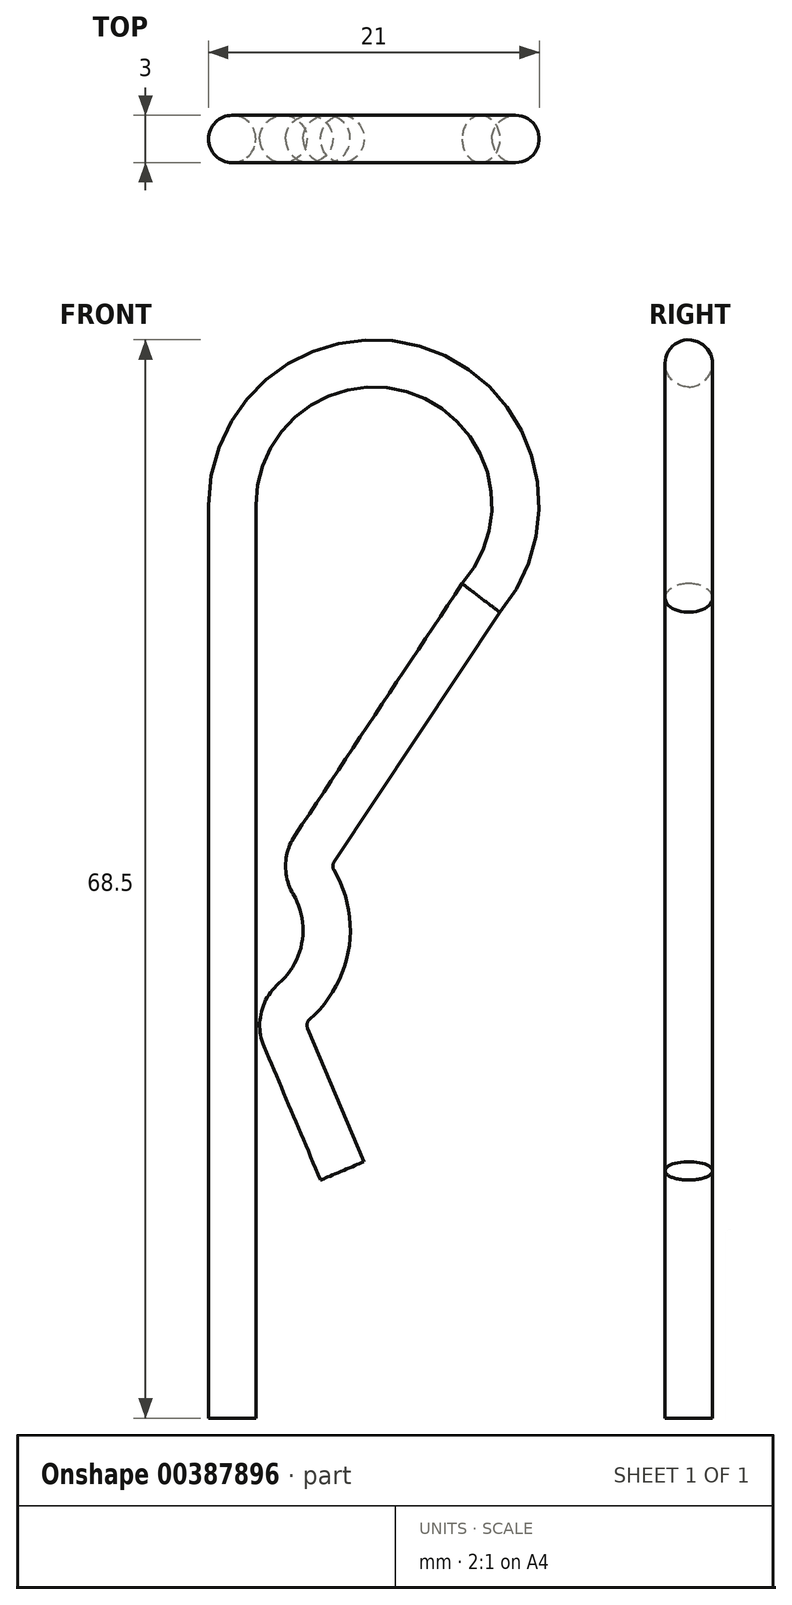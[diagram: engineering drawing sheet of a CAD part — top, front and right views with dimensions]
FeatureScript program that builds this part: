
annotation { "Feature Type Name" : "Feature", "Feature Type Description" : "" }
export const myFeature = defineFeature(function(context is Context, id is Id, definition is map)
    precondition{}
    {
        {
            var Q0;
            Q0=qCreatedBy(makeId("Front.planeOp"),FACE);
            var sketch = newSketch(context, id + "F0", { "sketchPlane" : qUnion([Q0])});
            skArc(sketch, "E0", {"start": v(15.8, 52.1) * mm, "mid": v(12.15, 66.43) * mm, "end": v(0, 58) * mm});
            skLineSegment(sketch, "E1", {"start": v(15.8, 52.1) * mm, "end": v(5.22, 36.17) * mm});
            skLineSegment(sketch, "E2", {"start": v(3.4, 24.18) * mm, "end": v(7, 15.7) * mm});
            skArc(sketch, "E3", {"start": v(3.94, 26.47) * mm, "mid": v(5.92, 30.04) * mm, "end": v(5.17, 34.05) * mm});
            skPoint(sketch, "E4.visualSharp", {"position": v(4.46, 35.01) * mm});
            skArc(sketch, "E4.filletArc", {"start": v(5.22, 36.17) * mm, "mid": v(4.9, 35.12) * mm, "end": v(5.17, 34.05) * mm});
            skPoint(sketch, "E5.visualSharp", {"position": v(2.77, 25.68) * mm});
            skArc(sketch, "E5.filletArc", {"start": v(3.94, 26.47) * mm, "mid": v(3.3, 25.41) * mm, "end": v(3.4, 24.18) * mm});
            skLineSegment(sketch, "E6", {"start": v(0, 58) * mm, "end": v(0, 0) * mm});
            skSolve(sketch);
        }
        {
            var Q0;
            Q0=qCreatedBy(makeId("Top.planeOp"),FACE);
            var sketch = newSketch(context, id + "F1", { "sketchPlane" : qUnion([Q0])});
            skCircle(sketch, "E7", {"center": v(0, 0) * mm, "radius": 1.5 * mm});
            skSolve(sketch);
        }
        {
            var Q0;
            Q0=makeQuery(id+"F1.imprint","IMPRINT",FACE,{"disambiguationData":[TD([[makeQuery(id+"F1.imprint","IMPRINT",EDGE,{"derivedFrom":sQuery(id+"F1.wireOp",EDGE,"E7")}),1.0]])]});
            var Q1;
            Q1=sQuery(id+"F0.wireOp",EDGE,"E6");
            var Q2;
            Q2=sQuery(id+"F0.wireOp",EDGE,"E0");
            var Q3;
            Q3=sQuery(id+"F0.wireOp",EDGE,"E1");
            var Q4;
            Q4=sQuery(id+"F0.wireOp",EDGE,"E4.filletArc");
            var Q5;
            Q5=sQuery(id+"F0.wireOp",EDGE,"E3");
            var Q6;
            Q6=sQuery(id+"F0.wireOp",EDGE,"E5.filletArc");
            var Q7;
            Q7=sQuery(id+"F0.wireOp",EDGE,"E2");
            sweep(context, id + "F2", {"profiles" : qUnion([Q0]), "path" : qUnion([Q1, Q2, Q3, Q4, Q5, Q6, Q7])});
        }
    });
